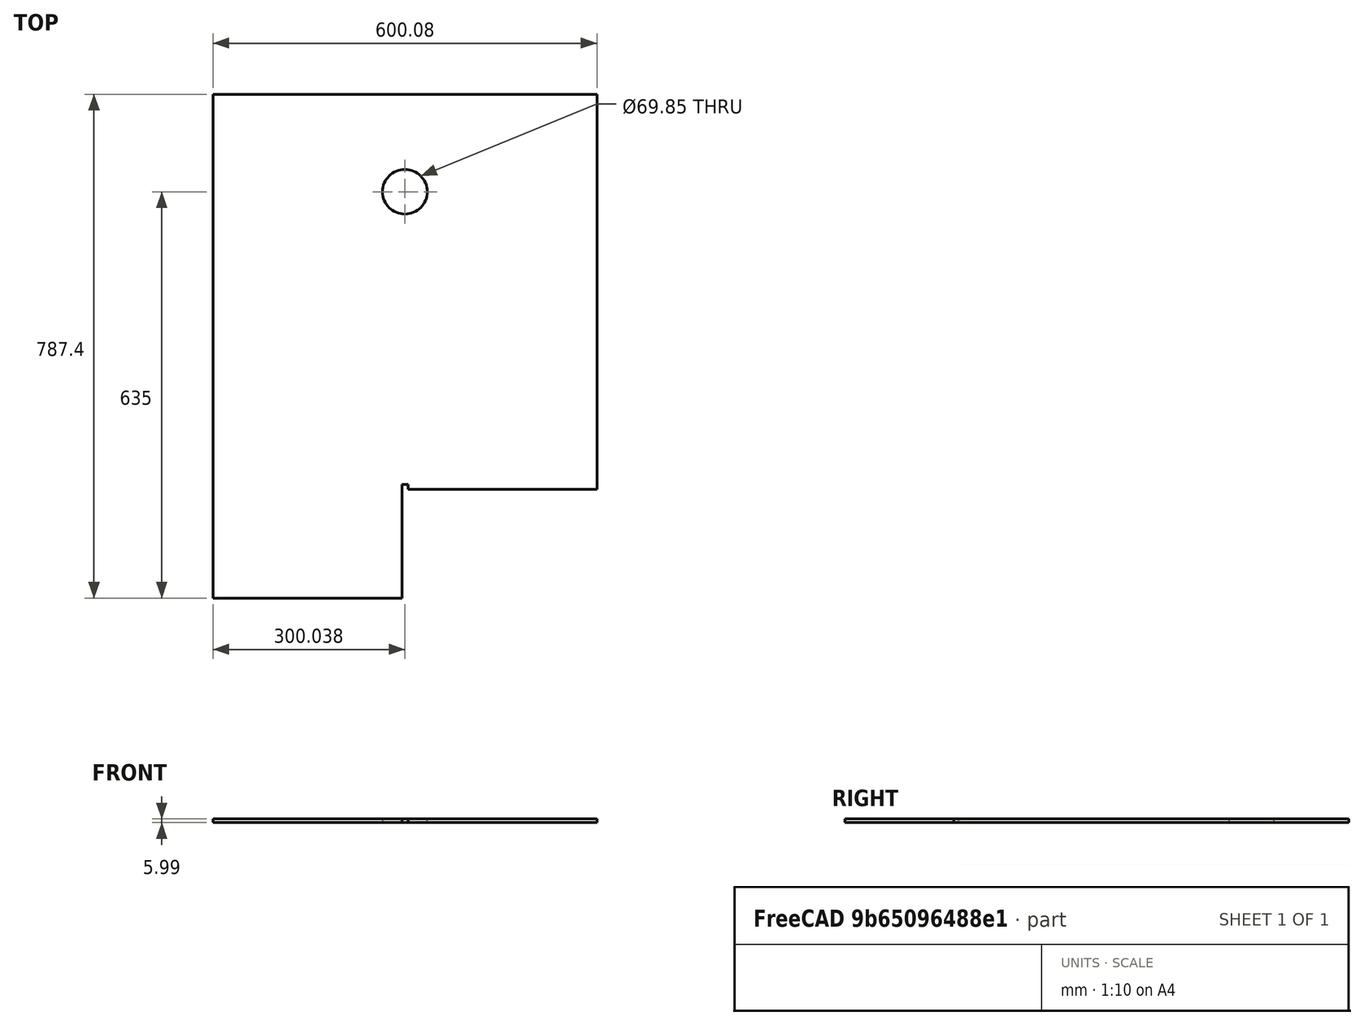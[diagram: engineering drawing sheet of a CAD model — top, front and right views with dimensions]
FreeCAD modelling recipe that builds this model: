
FCSTD DOCUMENT  (FreeCAD 0.19R24267 (Git))
Label: Inv2-P8
License: All rights reserved
LicenseURL: http://en.wikipedia.org/wiki/All_rights_reserved
objects: TechDraw::DrawViewDimension×11, TechDraw::DrawProjGroupItem×2, TechDraw::DrawHatch×2, TechDraw::DrawViewAnnotation×2, Sketcher::SketchObject×1, Part::Extrusion×1, TechDraw::DrawSVGTemplate×1, TechDraw::DrawProjGroup×1, TechDraw::DrawPage×1
note: 2 computed .brp shape members not serialized (recipe doc carries the construction recipe); baked Part::Feature solids carry a one-line shape summary decoded from their .brp

FEATURE [Sketcher::SketchObject] Sketch
  FullyConstrained = true
  sketch-geometry (10):
    g0: LineSegment StartX=0 StartY=0 StartZ=0 EndX=600.075 EndY=0 EndZ=0
    g1: LineSegment StartX=600.075 StartY=0 StartZ=0 EndX=600.075 EndY=-617.55 EndZ=0
    g2: LineSegment StartX=295.275 StartY=-609.6 StartZ=0 EndX=295.275 EndY=-787.4 EndZ=0
    g3: LineSegment StartX=295.275 StartY=-787.4 StartZ=0 EndX=0 EndY=-787.4 EndZ=0
    g4: LineSegment StartX=0 StartY=-787.4 StartZ=0 EndX=0 EndY=0 EndZ=0
    g5: Circle CenterX=300.037 CenterY=-152.4 CenterZ=0 NormalX=0 NormalY=0 NormalZ=1 AngleXU=0 Radius=34.925
    g6: LineSegment StartX=300.038 StartY=0 StartZ=0 EndX=300.038 EndY=-609.6 EndZ=0
    g7: LineSegment StartX=295.275 StartY=-609.6 StartZ=0 EndX=304.8 EndY=-609.6 EndZ=0
    g8: LineSegment StartX=304.8 StartY=-609.6 StartZ=0 EndX=304.8 EndY=-617.55 EndZ=0
    g9: LineSegment StartX=304.8 StartY=-617.55 StartZ=0 EndX=600.075 EndY=-617.55 EndZ=0
  constraints (29):
    c: Coincident(g0,g-1)
    c: PointOnObject(g0,g-1)
    c: Coincident(g1,g0)
    c: Vertical(g1)
    c: Vertical(g2)
    c: Coincident(g3,g2)
    c: PointOnObject(g3,g-2)
    c: Horizontal(g3)
    c: Coincident(g4,g3)
    c: Coincident(g4,g0)
    c: Distance(g0,g1) = 600.075
    c: Distance(g0,g3) = 787.4
    c: Distance(g3,g2) = 295.275
    c: Diameter(g5) = 69.85
    c: PointOnObject(g6,g0)
    c: Symmetric(g0,g0,g6)
    c: PointOnObject(g5,g6)
    c: Distance(g5,g0) = 152.4
    c: Coincident(g7,g2)
    c: Horizontal(g7)
    c: Coincident(g8,g7)
    c: Vertical(g8)
    c: Coincident(g9,g8)
    c: Horizontal(g9)
    c: Distance(g2) = 177.8
    c: Distance(g8) = 7.9502
    c: Distance(g7) = 9.525
    c: Coincident(g9,g1)
    c: PointOnObject(g6,g7)
FEATURE [Part::Extrusion] Extrude
  Base = -> Sketch
  Dir = (0,0,1)
  DirMode = 2
  FaceMakerClass = Part::FaceMakerBullseye
  LengthFwd = 5.9944
  LengthRev = 0
  Solid = true
  Symmetric = false
FEATURE [TechDraw::DrawSVGTemplate] Template
  Height = 215.9
  Orientation = 1
  Width = 279.4
FEATURE [TechDraw::DrawProjGroupItem] ProjItem  label="Front"
  CoarseView = false
  Direction = (0,0,1)
  Focus = 100
  HardHidden = false
  IsoCount = 0
  IsoHidden = false
  IsoVisible = false
  LockPosition = true
  Perspective = false
  Rotation = 0
  RotationVector = (1,0,0)
  Scale = 0.2
  ScaleType = 2
  SeamHidden = false
  SeamVisible = true
  SmoothHidden = false
  SmoothVisible = true
  Source = -> [Extrude]
  Type = 0
  X = 0
  XDirection = (1,0,0)
  Y = 0
FEATURE [TechDraw::DrawProjGroupItem] ProjItem001  label="Left"
  CoarseView = false
  Direction = (-1,0,1e-16)
  Focus = 100
  HardHidden = false
  IsoCount = 0
  IsoHidden = false
  IsoVisible = false
  LockPosition = false
  Perspective = false
  Rotation = 0
  RotationVector = (1,0,0)
  Scale = 0.2
  ScaleType = 2
  SeamHidden = false
  SeamVisible = true
  SmoothHidden = false
  SmoothVisible = true
  Source = -> [Extrude]
  Type = 1
  X = 84.0009
  XDirection = (1e-16,0,1)
  Y = 0
FEATURE [TechDraw::DrawProjGroup] ProjGroup
  Anchor = -> ProjItem
  AutoDistribute = true
  LockPosition = false
  ProjectionType = 0
  Rotation = 0
  Scale = 0.2
  ScaleType = 2
  Source = -> [Extrude]
  Views = -> [ProjItem,ProjItem001]
  X = 148.548
  Y = 104.861
  spacingX = 15.0114
  spacingY = 15.0114
FEATURE [TechDraw::DrawHatch] Hatch  label="HatchF0"
  HatchPattern = <path>
  Source = -> ProjItem [Face0]
FEATURE [TechDraw::DrawHatch] Hatch001  label="Hatch001F0"
  HatchPattern = <path>
  Source = -> ProjItem001 [Face0]
FEATURE [TechDraw::DrawViewDimension] Dimension
  Arbitrary = false
  ArbitraryTolerances = false
  EqualTolerance = true
  FormatSpec = ⌀%.3f
  FormatSpecOverTolerance = %+.3f
  FormatSpecUnderTolerance = %+.3f
  Inverted = false
  LockPosition = false
  MeasureType = 1
  OverTolerance = 0
  References2D = -> [ProjItem]
  Rotation = 0
  ScaleType = 0
  TheoreticalExact = false
  Type = 5
  UnderTolerance = 0
  X = -17.335
  Y = 68.2478
FEATURE [TechDraw::DrawViewDimension] Dimension001
  Arbitrary = false
  ArbitraryTolerances = false
  EqualTolerance = true
  FormatSpec = %.3f
  FormatSpecOverTolerance = %+.3f
  FormatSpecUnderTolerance = %+.3f
  Inverted = false
  LockPosition = false
  MeasureType = 1
  OverTolerance = 0
  References2D = -> [ProjItem]
  Rotation = 0
  ScaleType = 0
  TheoreticalExact = false
  Type = 2
  UnderTolerance = 0
  X = 24.5194
  Y = 61.1902
FEATURE [TechDraw::DrawViewDimension] Dimension002
  Arbitrary = false
  ArbitraryTolerances = false
  EqualTolerance = true
  FormatSpec = %.3f
  FormatSpecOverTolerance = %+.3f
  FormatSpecUnderTolerance = %+.3f
  Inverted = false
  LockPosition = false
  MeasureType = 1
  OverTolerance = 0
  References2D = -> [ProjItem]
  Rotation = 0
  ScaleType = 0
  TheoreticalExact = false
  Type = 1
  UnderTolerance = 0
  X = -29.1928
  Y = 37.1766
FEATURE [TechDraw::DrawViewDimension] Dimension003
  Arbitrary = false
  ArbitraryTolerances = false
  EqualTolerance = true
  FormatSpec = %.3f
  FormatSpecOverTolerance = %+.3f
  FormatSpecUnderTolerance = %+.3f
  Inverted = false
  LockPosition = false
  MeasureType = 1
  OverTolerance = 0
  References2D = -> [ProjItem]
  Rotation = 0
  ScaleType = 0
  TheoreticalExact = false
  Type = 1
  UnderTolerance = 0
  X = 0
  Y = 94.1162
FEATURE [TechDraw::DrawViewDimension] Dimension004
  Arbitrary = false
  ArbitraryTolerances = false
  EqualTolerance = true
  FormatSpec = %.3f
  FormatSpecOverTolerance = %+.3f
  FormatSpecUnderTolerance = %+.3f
  Inverted = false
  LockPosition = false
  MeasureType = 1
  OverTolerance = 0
  References2D = -> [ProjItem]
  Rotation = 0
  ScaleType = 0
  TheoreticalExact = false
  Type = 2
  UnderTolerance = 0
  X = -83.8308
  Y = 3.36329
FEATURE [TechDraw::DrawViewDimension] Dimension005
  Arbitrary = false
  ArbitraryTolerances = false
  EqualTolerance = true
  FormatSpec = %.3f
  FormatSpecOverTolerance = %+.3f
  FormatSpecUnderTolerance = %+.3f
  Inverted = false
  LockPosition = false
  MeasureType = 1
  OverTolerance = 0
  References2D = -> [ProjItem]
  Rotation = 0
  ScaleType = 0
  TheoreticalExact = false
  Type = 1
  UnderTolerance = 0
  X = 30.1779
  Y = -23.8411
FEATURE [TechDraw::DrawViewDimension] Dimension006
  Arbitrary = false
  ArbitraryTolerances = false
  EqualTolerance = true
  FormatSpec = %.3f
  FormatSpecOverTolerance = %+.3f
  FormatSpecUnderTolerance = %+.3f
  Inverted = false
  LockPosition = false
  MeasureType = 1
  OverTolerance = 0
  References2D = -> [ProjItem]
  Rotation = 0
  ScaleType = 0
  TheoreticalExact = false
  Type = 2
  UnderTolerance = 0
  X = 18.2178
  Y = -61.4747
FEATURE [TechDraw::DrawViewDimension] Dimension007
  Arbitrary = false
  ArbitraryTolerances = false
  EqualTolerance = true
  FormatSpec = %.3f
  FormatSpecOverTolerance = %+.3f
  FormatSpecUnderTolerance = %+.3f
  Inverted = false
  LockPosition = false
  MeasureType = 1
  OverTolerance = 0
  References2D = -> [ProjItem]
  Rotation = 0
  ScaleType = 0
  TheoreticalExact = false
  Type = 1
  UnderTolerance = 0
  X = -29.8342
  Y = -23.8057
FEATURE [TechDraw::DrawViewDimension] Dimension008
  Arbitrary = false
  ArbitraryTolerances = false
  EqualTolerance = true
  FormatSpec = %.3f
  FormatSpecOverTolerance = %+.3f
  FormatSpecUnderTolerance = %+.3f
  Inverted = false
  LockPosition = false
  MeasureType = 1
  OverTolerance = 0
  References2D = -> [ProjItem]
  Rotation = 0
  ScaleType = 0
  TheoreticalExact = false
  Type = 2
  UnderTolerance = 0
  X = 9.54509
  Y = -50.8141
FEATURE [TechDraw::DrawViewDimension] Dimension009
  Arbitrary = false
  ArbitraryTolerances = false
  EqualTolerance = true
  FormatSpec = %.3f
  FormatSpecOverTolerance = %+.3f
  FormatSpecUnderTolerance = %+.3f
  Inverted = false
  LockPosition = false
  MeasureType = 1
  OverTolerance = 0
  References2D = -> [ProjItem]
  Rotation = 0
  ScaleType = 0
  TheoreticalExact = false
  Type = 1
  UnderTolerance = 0
  X = -15.1815
  Y = -35.9785
FEATURE [TechDraw::DrawViewDimension] Dimension010
  Arbitrary = false
  ArbitraryTolerances = false
  EqualTolerance = true
  FormatSpec = %.3f
  FormatSpecOverTolerance = %+.3f
  FormatSpecUnderTolerance = %+.3f
  Inverted = false
  LockPosition = false
  MeasureType = 1
  OverTolerance = 0
  References2D = -> [ProjItem001]
  Rotation = 0
  ScaleType = 0
  TheoreticalExact = false
  Type = 1
  UnderTolerance = 0
  X = 12.5933
  Y = 73.734
FEATURE [TechDraw::DrawViewAnnotation] Annotation
  Font = osifont
  LineSpace = 80
  LockPosition = false
  MaxWidth = -1
  Rotation = 0
  ScaleType = 0
  Text = Figure S2 (Inverted 2) | Panel 8 [left side exterior baffle] | Quantity: 1
  TextSize = 5.0038
  TextStyle = 0
  X = 46.2149
  Y = 195.58
FEATURE [TechDraw::DrawViewAnnotation] Annotation002
  Font = osifont
  LineSpace = 80
  LockPosition = false
  MaxWidth = -1
  Rotation = 0
  ScaleType = 0
  Text = Units: Inches
  TextSize = 5.0038
  TextStyle = 0
  X = 259.08
  Y = 5.08
FEATURE [TechDraw::DrawPage] Page
  KeepUpdated = true
  NextBalloonIndex = 1
  ProjectionType = 0
  Template = -> Template
  Views = -> [ProjGroup,Dimension,Dimension001,Dimension002,Dimension003,Dimension004,Dimension005,Dimension006,Dimension007,Dimension008,Dimension009,Dimension010,Annotation,Annotation002]
note: 2 file-system paths scrubbed to <path> (originals preserved in the JSON sidecar)
